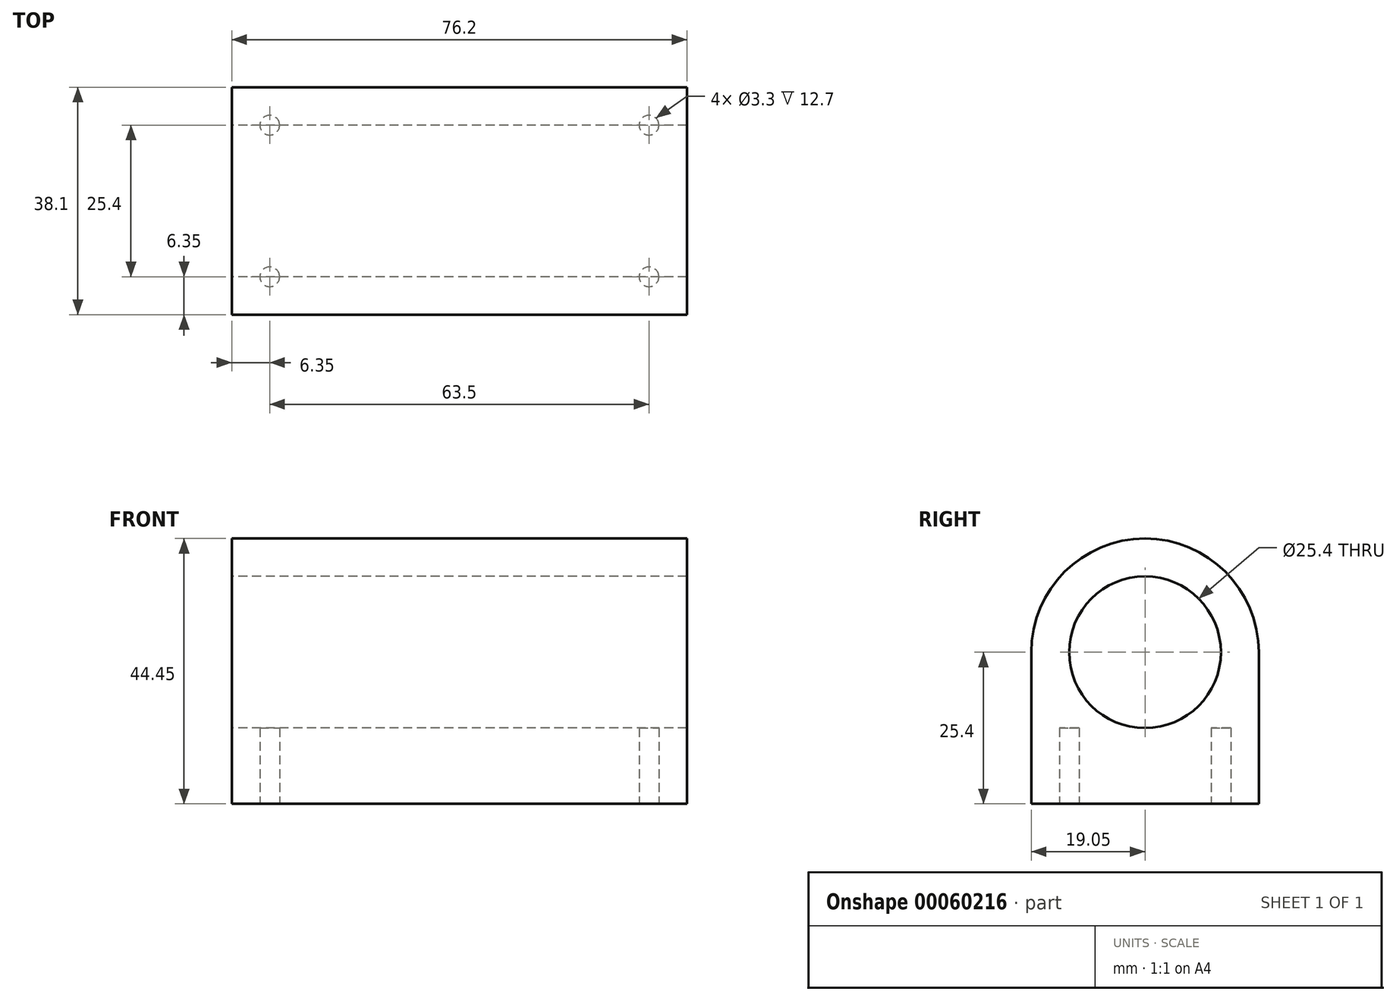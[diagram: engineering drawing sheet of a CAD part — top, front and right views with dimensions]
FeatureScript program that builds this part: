
annotation { "Feature Type Name" : "Feature", "Feature Type Description" : "" }
export const myFeature = defineFeature(function(context is Context, id is Id, definition is map)
    precondition{}
    {
        {
            var Q0;
            Q0=qCreatedBy(makeId("Right.planeOp"),FACE);
            var sketch = newSketch(context, id + "F0", { "sketchPlane" : qUnion([Q0])});
            skCircle(sketch, "E0", {"center": v(0, 0) * mm, "radius": 12.7 * mm});
            skArc(sketch, "E1", {"start": v(19.05, 0) * mm, "mid": v(0, 19.05) * mm, "end": v(-19.05, 0) * mm});
            skLineSegment(sketch, "E2", {"start": v(19.05, 0) * mm, "end": v(19.05, -25.4) * mm});
            skLineSegment(sketch, "E3", {"start": v(-19.05, 0) * mm, "end": v(-19.05, -25.4) * mm});
            skLineSegment(sketch, "E4", {"start": v(-19.05, -25.4) * mm, "end": v(19.05, -25.4) * mm});
            skSolve(sketch);
        }
        {
            var Q0;
            Q0 = qSketchRegion(id + "F0", true);
            extrude(context, id + "F1", {"entities" : qUnion([Q0]), "depth" : 76.2 * mm});
        }
        {
            var Q0;
            Q0=makeQuery(id+"F1.opExtrude","SWEPT_FACE",FACE,{"disambiguationData":[OSD([sQuery(id+"F0.wireOp",EDGE,"E4")])]});
            var sketch = newSketch(context, id + "F2", { "sketchPlane" : qUnion([Q0])});
            skCircle(sketch, "E5", {"center": v(6.35, 12.7) * mm, "radius": 1.65 * mm});
            skCircle(sketch, "E6", {"center": v(69.85, 12.7) * mm, "radius": 1.65 * mm});
            skCircle(sketch, "E7", {"center": v(69.85, -12.7) * mm, "radius": 1.65 * mm});
            skCircle(sketch, "E8", {"center": v(6.35, -12.7) * mm, "radius": 1.65 * mm});
            skSolve(sketch);
        }
        {
            var Q0;
            Q0 = qSketchRegion(id + "F2", true);
            extrude(context, id + "F3", {"entities" : qUnion([Q0]), "operationType" : NewBodyOperationType.REMOVE, "oppositeDirection" : true, "depth" : 12.7 * mm});
        }
    });
